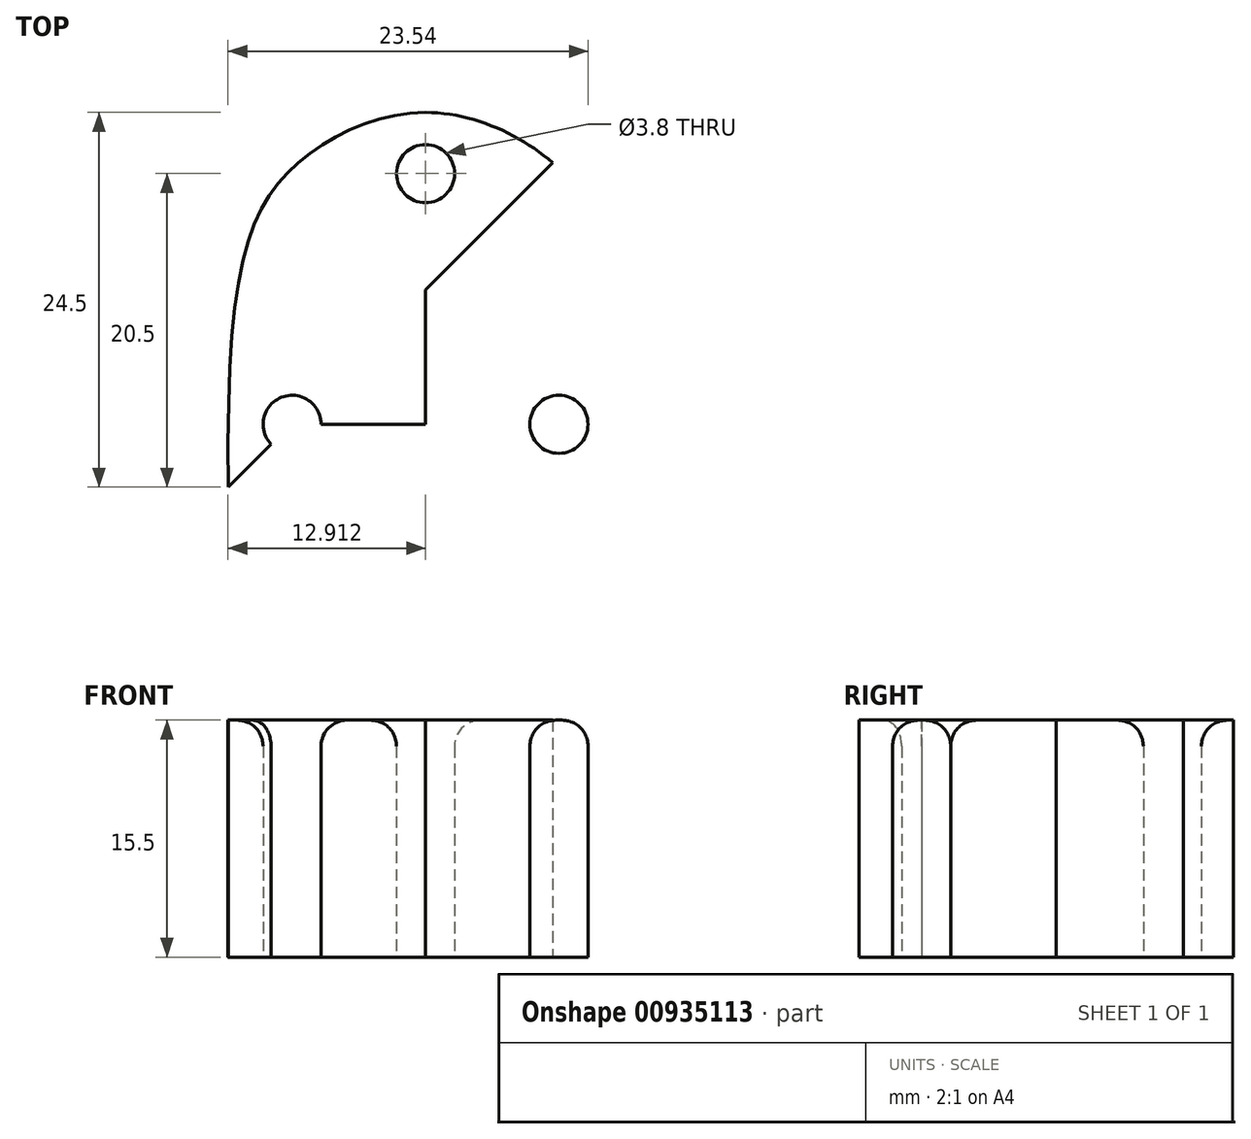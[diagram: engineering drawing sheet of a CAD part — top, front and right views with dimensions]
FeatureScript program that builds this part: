
annotation { "Feature Type Name" : "Feature", "Feature Type Description" : "" }
export const myFeature = defineFeature(function(context is Context, id is Id, definition is map)
    precondition{}
    {
        {
            var Q0;
            Q0=qCreatedBy(makeId("Top.planeOp"),FACE);
            var sketch = newSketch(context, id + "F0", { "sketchPlane" : qUnion([Q0])});
            skLineSegment(sketch, "E0", {"start": v(-29.5, 0) * mm, "end": v(-3.7, 0) * mm});
            skFitSpline(sketch, "E1", {"points": [v(-29.5, 0) * mm, v(-24.91, 21.21) * mm, v(-16.6, 24.5) * mm, v(-8.28, 21.21) * mm, v(-3.7, 0) * mm], "startDerivative": vector(-1.54, 139.2) * mm, "endDerivative": vector(-1.54, -139.2) * mm});
            skLineSegment(sketch, "E2", {"start": v(-16.6, 0) * mm, "end": v(-16.6, 24.5) * mm});
            skLineSegment(sketch, "E3", {"start": v(-29.5, 0) * mm, "end": v(-8.28, 21.21) * mm});
            skLineSegment(sketch, "E4", {"start": v(-25.32, 4.1) * mm, "end": v(-7.87, 4.1) * mm});
            skLineSegment(sketch, "E5", {"start": v(-16.6, 0) * mm, "end": v(-16.6, 4.1) * mm});
            skCircle(sketch, "E6", {"center": v(-25.32, 4.1) * mm, "radius": 1.9 * mm});
            skCircle(sketch, "E7", {"center": v(-7.87, 4.1) * mm, "radius": 1.9 * mm});
            skCircle(sketch, "E8", {"center": v(-16.6, 20.5) * mm, "radius": 1.9 * mm});
            skLineSegment(sketch, "E9", {"start": v(-16.6, 24.5) * mm, "end": v(-16.6, 20.5) * mm});
            skSolve(sketch);
        }
        {
            var Q0;
            {var subQ0=sQuery(id+"F0.wireOp",EDGE,"E3");var subQ1=sQuery(id+"F0.wireOp",EDGE,"E2");var subQ2=makeQuery(id+"F0.imprint","INTERSECT",VERTEX,{"derivedFrom":[subQ1,subQ0]});Q0=makeQuery(id+"F0.imprint","IMPRINT",FACE,{"disambiguationData":[TD([[makeQuery(id+"F0.imprint","IMPRINT",EDGE,{"disambiguationData":[TD([[subQ2,-1.0]])],"derivedFrom":subQ1}),1.0]])]});}
            var Q1;
            {var subQ5=sQuery(id+"F0.wireOp",EDGE,"E3");var subQ6=sQuery(id+"F0.wireOp",EDGE,"E1");var subQ7=makeQuery(id+"F0.imprint","INTERSECT",VERTEX,{"derivedFrom":[subQ6,subQ5]});Q1=makeQuery(id+"F0.imprint","IMPRINT",FACE,{"disambiguationData":[TD([[makeQuery(id+"F0.imprint","IMPRINT",EDGE,{"disambiguationData":[TD([[subQ7,1.0]])],"derivedFrom":subQ6}),-1.0]])]});}
            var Q2;
            {var subQ0=sQuery(id+"F0.wireOp",EDGE,"E9");var subQ1=sQuery(id+"F0.wireOp",EDGE,"E2");var subQ2=makeQuery(id+"F0.imprint","INTERSECT",VERTEX,{"derivedFrom":[subQ1,subQ0]});Q2=makeQuery(id+"F0.imprint","IMPRINT",FACE,{"disambiguationData":[TD([[makeQuery(id+"F0.imprint","IMPRINT",EDGE,{"disambiguationData":[TD([[subQ2,1.0]])],"derivedFrom":subQ1}),-1.0]])]});}
            var Q3;
            {var subQ0=sQuery(id+"F0.wireOp",EDGE,"E9");var subQ1=sQuery(id+"F0.wireOp",EDGE,"E2");var subQ2=makeQuery(id+"F0.imprint","INTERSECT",VERTEX,{"derivedFrom":[subQ1,subQ0]});Q3=makeQuery(id+"F0.imprint","IMPRINT",FACE,{"disambiguationData":[TD([[makeQuery(id+"F0.imprint","IMPRINT",EDGE,{"disambiguationData":[TD([[subQ2,1.0]])],"derivedFrom":subQ1}),1.0]])]});}
            var Q4;
            {var subQ0=sQuery(id+"F0.wireOp",EDGE,"E5");Q4=makeQuery(id+"F0.imprint","IMPRINT",FACE,{"disambiguationData":[TD([[makeQuery(id+"F0.imprint","IMPRINT",EDGE,{"derivedFrom":subQ0}),-1.0]])]});}
            var Q5;
            Q5=makeQuery(id+"F0.imprint","IMPRINT",FACE,{"disambiguationData":[TD([[makeQuery(id+"F0.imprint","IMPRINT",EDGE,{"derivedFrom":sQuery(id+"F0.wireOp",EDGE,"E7")}),1.0]])]});
            var Q6;
            {var subQ1=sQuery(id+"F0.wireOp",EDGE,"E2");var subQ3=sQuery(id+"F0.wireOp",EDGE,"E3");var subQ4=makeQuery(id+"F0.imprint","INTERSECT",VERTEX,{"derivedFrom":[subQ1,subQ3]});Q6=makeQuery(id+"F0.imprint","IMPRINT",FACE,{"disambiguationData":[TD([[makeQuery(id+"F0.imprint","IMPRINT",EDGE,{"disambiguationData":[TD([[subQ4,1.0]])],"derivedFrom":subQ3}),-1.0]])]});}
            var Q7;
            {var subQ0=sQuery(id+"F0.wireOp",EDGE,"E5");Q7=makeQuery(id+"F0.imprint","IMPRINT",FACE,{"disambiguationData":[TD([[makeQuery(id+"F0.imprint","IMPRINT",EDGE,{"derivedFrom":subQ0}),1.0]])]});}
            var Q8;
            {var subQ0=sQuery(id+"F0.wireOp",EDGE,"E6");var subQ1=sQuery(id+"F0.wireOp",EDGE,"E3");var subQ2=makeQuery(id+"F0.imprint","INTERSECT",VERTEX,{"disambiguationData":[OD(0.0)],"derivedFrom":[subQ1,subQ0]});Q8=makeQuery(id+"F0.imprint","IMPRINT",FACE,{"disambiguationData":[TD([[makeQuery(id+"F0.imprint","IMPRINT",EDGE,{"disambiguationData":[TD([[subQ2,-1.0]])],"derivedFrom":subQ1}),-1.0]])]});}
            var Q9;
            {var subQ0=sQuery(id+"F0.wireOp",EDGE,"E6");var subQ1=sQuery(id+"F0.wireOp",EDGE,"E3");var subQ2=makeQuery(id+"F0.imprint","INTERSECT",VERTEX,{"disambiguationData":[OD(0.0)],"derivedFrom":[subQ1,subQ0]});Q9=makeQuery(id+"F0.imprint","IMPRINT",FACE,{"disambiguationData":[TD([[makeQuery(id+"F0.imprint","IMPRINT",EDGE,{"disambiguationData":[TD([[subQ2,-1.0]])],"derivedFrom":subQ1}),1.0]])]});}
            extrude(context, id + "F1", {"entities" : qUnion([Q0, Q1, Q2, Q3, Q4, Q5, Q6, Q7, Q8, Q9]), "depth" : 5.5 * mm, "offsetDistance" : 25 * mm});
        }
        {
            var Q0;
            {var subQ0=sQuery(id+"F0.wireOp",EDGE,"E6");var subQ1=sQuery(id+"F0.wireOp",EDGE,"E3");var subQ2=makeQuery(id+"F0.imprint","INTERSECT",VERTEX,{"disambiguationData":[OD(0.0)],"derivedFrom":[subQ1,subQ0]});Q0=makeQuery(id+"F0.imprint","IMPRINT",FACE,{"disambiguationData":[TD([[makeQuery(id+"F0.imprint","IMPRINT",EDGE,{"disambiguationData":[TD([[subQ2,-1.0]])],"derivedFrom":subQ1}),1.0]])]});}
            var Q1;
            {var subQ0=sQuery(id+"F0.wireOp",EDGE,"E6");var subQ1=sQuery(id+"F0.wireOp",EDGE,"E3");var subQ2=makeQuery(id+"F0.imprint","INTERSECT",VERTEX,{"disambiguationData":[OD(0.0)],"derivedFrom":[subQ1,subQ0]});Q1=makeQuery(id+"F0.imprint","IMPRINT",FACE,{"disambiguationData":[TD([[makeQuery(id+"F0.imprint","IMPRINT",EDGE,{"disambiguationData":[TD([[subQ2,-1.0]])],"derivedFrom":subQ1}),-1.0]])]});}
            var Q2;
            {var subQ0=sQuery(id+"F0.wireOp",EDGE,"E9");var subQ1=sQuery(id+"F0.wireOp",EDGE,"E2");var subQ2=makeQuery(id+"F0.imprint","INTERSECT",VERTEX,{"derivedFrom":[subQ1,subQ0]});Q2=makeQuery(id+"F0.imprint","IMPRINT",FACE,{"disambiguationData":[TD([[makeQuery(id+"F0.imprint","IMPRINT",EDGE,{"disambiguationData":[TD([[subQ2,1.0]])],"derivedFrom":subQ1}),-1.0]])]});}
            var Q3;
            {var subQ0=sQuery(id+"F0.wireOp",EDGE,"E9");var subQ1=sQuery(id+"F0.wireOp",EDGE,"E2");var subQ2=makeQuery(id+"F0.imprint","INTERSECT",VERTEX,{"derivedFrom":[subQ1,subQ0]});Q3=makeQuery(id+"F0.imprint","IMPRINT",FACE,{"disambiguationData":[TD([[makeQuery(id+"F0.imprint","IMPRINT",EDGE,{"disambiguationData":[TD([[subQ2,1.0]])],"derivedFrom":subQ1}),1.0]])]});}
            var Q4;
            Q4=makeQuery(id+"F0.imprint","IMPRINT",FACE,{"disambiguationData":[TD([[makeQuery(id+"F0.imprint","IMPRINT",EDGE,{"derivedFrom":sQuery(id+"F0.wireOp",EDGE,"E7")}),1.0]])]});
            extrude(context, id + "F2", {"entities" : qUnion([Q0, Q1, Q2, Q3, Q4]), "operationType" : NewBodyOperationType.ADD, "depth" : 15.5 * mm, "offsetDistance" : 25 * mm});
        }
        {
            var Q0;
            Q0=makeQuery(id+"F2.opExtrude","CAP_EDGE",EDGE,{"disambiguationData":[OSD([sQuery(id+"F0.wireOp",EDGE,"E8")])],"isStart":false});
            var Q1;
            Q1=makeQuery(id+"F2.opExtrude","CAP_EDGE",EDGE,{"disambiguationData":[OSD([sQuery(id+"F0.wireOp",EDGE,"E6")])],"isStart":false});
            var Q2;
            Q2=makeQuery(id+"F2.opExtrude","CAP_EDGE",EDGE,{"disambiguationData":[OSD([sQuery(id+"F0.wireOp",EDGE,"E7")])],"isStart":false});
            fillet(context, id + "F3", {"entities" : qUnion([Q0, Q1, Q2]), "radius" : 1.7 * mm, "tangentPropagation" : true, "allowEdgeOverflow" : false});
        }
    });
